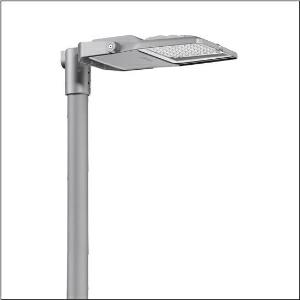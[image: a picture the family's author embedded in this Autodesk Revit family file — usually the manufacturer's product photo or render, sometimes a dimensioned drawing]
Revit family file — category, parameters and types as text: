
# Revit family: floodlight_fl_21_iq_mini___pl64_5xa7772b2e3a_76f3
name_source: partatom
category: Lighting Fixtures
units: mm (PartAtom-declared; Revit-internal decimal feet)

## family parameters
Cut with Voids When Loaded = No
Host = Face
Light Source = No
Part Type = Normal
Room Calculation Point = No
Round Connector Dimension = Use Diameter
Shared = No

## types (1)
- --- (1 x LED, 6020 lm, 45.5 W, 3000K)
    Apparent Load = 46 VA
    CIE Flux Codes = 28 80 98 100 100
    Color Rendering = 70
    Color Temperature = 3000K
    Default Elevation = 1800 mm
    Description = Floodlight FL 21 iQ mini, floodlight, primary light control with lens, of PMMA, primary optical cover: protective disc, of toughened safety glass, transparent, light distribution: PL64, light emission: direct distribution, installation type: surface-mounted, LED, High Power LED, rated luminous flux: 6.020lm, luminous efficacy: 132lm/W, light colour: 730, colour temperature: 3000K, control: Auto-Match, Temp-Guard, Night-Set, Smart-Wire, Desk-Remote (wireless, voltage-free reading and setting of iQ features in the workshop via application-optimized NFC function/RFID function), optimised constant luminous flux control (CLO 2.0), Light-Fading, Lumen-Switch, with terminal, 6-pole, mains connection: 220..240V, AC, 50/60Hz, start of lifetime: 46W, end of service life: 48W, reduction: 22W, luminaire housing, of diecast aluminium, powder-coated, Siteco® metallic grey (DB 702S), corrosivity category C5 mid according to DIN EN ISO 12944, sealing non-destructively replaceable, please order mast flange separately, mast bracket, of steel, galvanised, powder-coated, protection rating (complete): IP66, insulation class (complete): insulation class II (safety insulation), certification: CE, ENEC, VDE, protection symbol: D, impact resistance: IK08, permissible operating ambient temperature: -40..+40°C, permissible operating ambient temperature for outdoor applications: -40..+50°C, standard: DIN EN 12944, LABS conformity tested according to VDMA 24364:2018-05, packaging unit: 1 piece

Light Distribution: PL64
    Height = 70 mm
    Lamp = 1 x LED
    Lamp Light Flux = 6020 lm
    Lamp Power = 45.5 W
    Lamp count = 1
    Length = 485 mm
    Luminous efficacy = 132 lm/W
    Manufacturer = Siteco
    ModVariant = No
    Model = 5XA7772B2E3A
    Number of Poles = 1
    OnlyDefault = Yes
    Power Factor = 1
    Product Name = Floodlight FL 21 iQ mini | PL64
    Product group = floodlight | pylon annexe
    ProductGroupID = 6200
    Protection Class = Protection class II
    Protection Degree = IP 66
    RLX_Detail_Level = 1
    RLX_Emergency_Light_Flux = 0 lm
    RLX_Emergency_Type = 0
    RLX_Emergency_Type_DB = No
    RlxData = <blob elided: 101245 chars, md5=4d789fc8>
    Socket = socket
    Standby Power = 0 W
    System Light Flux = 6020 lm
    System Power = 46 W
    Type Comments = factory setting: luminous flux: 100 % | dim-lin: 254 | 463 mA
    Type Image = l_1007125.jpg
    URL = http://relux.com
    VarID = @adj_099201
    Voltage = 0 V
    Weight = 0.00 kg
    Width = 337 mm

## geometry (parser evidence)
native form markers: Blend x4, Sweep x12
no freeform markers — native parametric forms only
